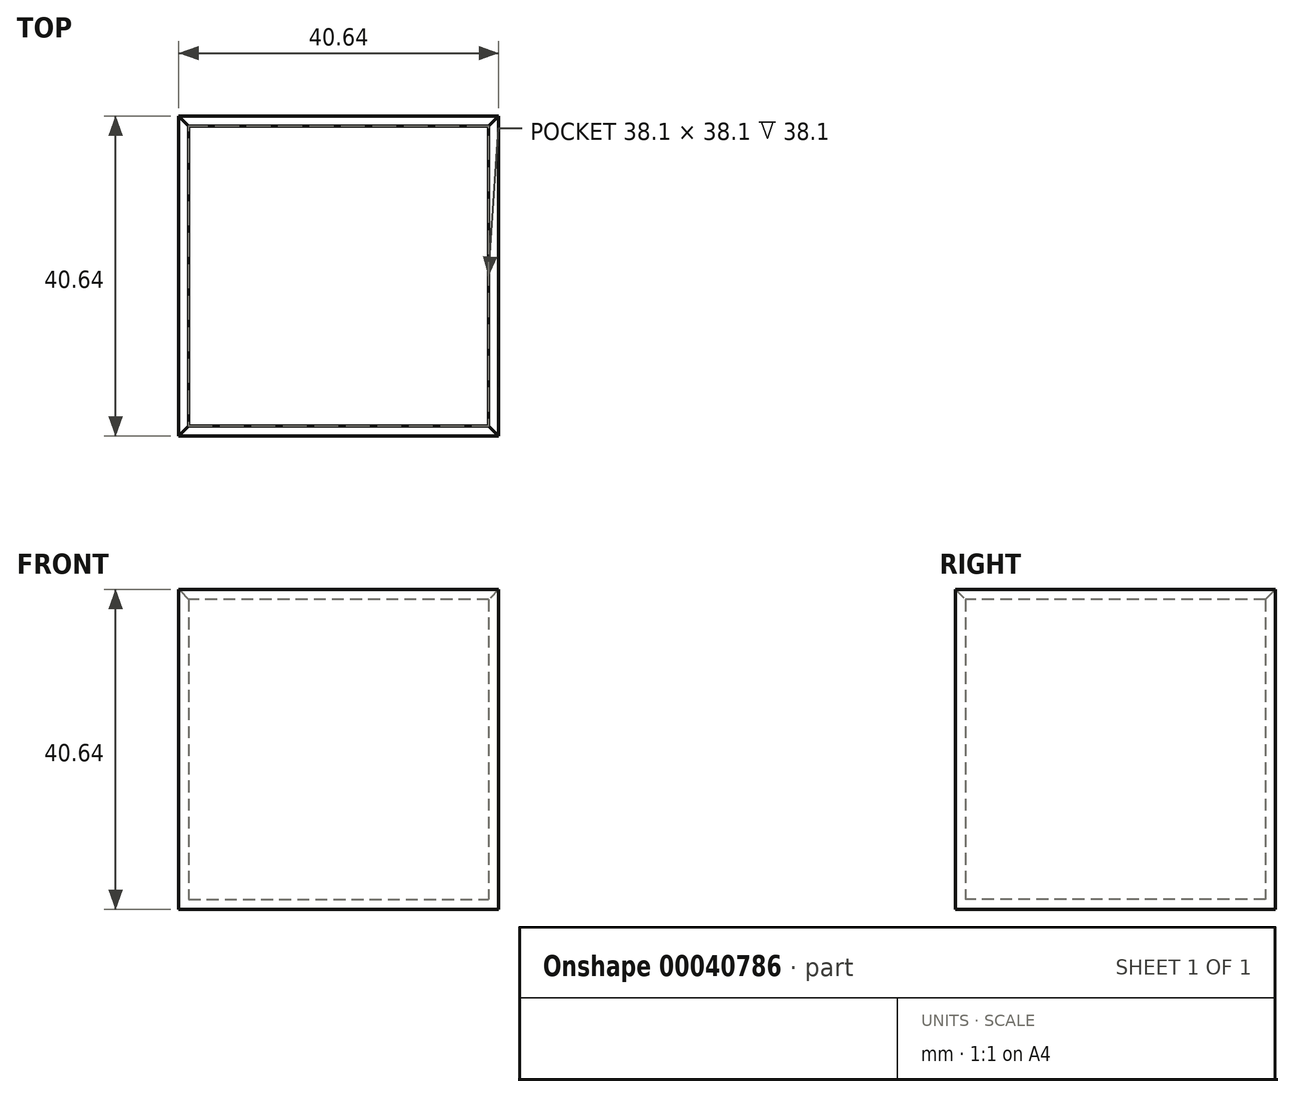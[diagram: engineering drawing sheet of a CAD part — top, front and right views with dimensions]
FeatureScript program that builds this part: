
annotation { "Feature Type Name" : "Feature", "Feature Type Description" : "" }
export const myFeature = defineFeature(function(context is Context, id is Id, definition is map)
    precondition{}
    {
        {
            var Q0;
            Q0=qCreatedBy(makeId("Top.planeOp"),FACE);
            var sketch = newSketch(context, id + "F0", { "sketchPlane" : qUnion([Q0])});
            skLineSegment(sketch, "E0.bottom", {"start": v(-21.61, 28.5) * mm, "end": v(19.03, 28.5) * mm});
            skLineSegment(sketch, "E0.top", {"start": v(-21.61, -12.14) * mm, "end": v(19.03, -12.14) * mm});
            skLineSegment(sketch, "E0.left", {"start": v(-21.61, 28.5) * mm, "end": v(-21.61, -12.14) * mm});
            skLineSegment(sketch, "E0.right", {"start": v(19.03, 28.5) * mm, "end": v(19.03, -12.14) * mm});
            skSolve(sketch);
        }
        {
            var Q0;
            Q0=makeQuery(id+"F0.imprint","IMPRINT",FACE,{"disambiguationData":[TD([[makeQuery(id+"F0.imprint","IMPRINT",EDGE,{"derivedFrom":sQuery(id+"F0.wireOp",EDGE,"E0.bottom")}),-1.0]])]});
            extrude(context, id + "F1", {"entities" : qUnion([Q0]), "depth" : 44.45 * mm});
        }
        {
            var Q0;
            Q0=makeQuery(id+"F1.opExtrude","CAP_FACE",FACE,{"disambiguationData":[OSD([sQuery(id+"F0.wireOp",EDGE,"E0.bottom"),sQuery(id+"F0.wireOp",EDGE,"E0.top"),sQuery(id+"F0.wireOp",EDGE,"E0.left"),sQuery(id+"F0.wireOp",EDGE,"E0.right")])],"isStart":false});
            shell(context, id + "F2", {"entities" : qUnion([Q0]), "thickness" : 1.27 * mm});
        }
        {
            var Q0;
            {var subQ0=sQuery(id+"F0.wireOp",EDGE,"E0.left");Q0=makeQuery(id+"F2.opShell","OFFSET_EDGE",EDGE,{"disambiguationData":[OSD([subQ0]),TDD([makeQuery(id+"F1.opExtrude","CAP_EDGE",EDGE,{"disambiguationData":[OSD([subQ0])],"isStart":false})])]});}
            var Q1;
            {var subQ0=sQuery(id+"F0.wireOp",EDGE,"E0.bottom");Q1=makeQuery(id+"F2.opShell","OFFSET_EDGE",EDGE,{"disambiguationData":[OSD([subQ0]),TDD([makeQuery(id+"F1.opExtrude","CAP_EDGE",EDGE,{"disambiguationData":[OSD([subQ0])],"isStart":false})])]});}
            var Q2;
            {var subQ0=sQuery(id+"F0.wireOp",EDGE,"E0.right");Q2=makeQuery(id+"F2.opShell","OFFSET_EDGE",EDGE,{"disambiguationData":[OSD([subQ0]),TDD([makeQuery(id+"F1.opExtrude","CAP_EDGE",EDGE,{"disambiguationData":[OSD([subQ0])],"isStart":false})])]});}
            var Q3;
            {var subQ0=sQuery(id+"F0.wireOp",EDGE,"E0.top");Q3=makeQuery(id+"F2.opShell","OFFSET_EDGE",EDGE,{"disambiguationData":[OSD([subQ0]),TDD([makeQuery(id+"F1.opExtrude","CAP_EDGE",EDGE,{"disambiguationData":[OSD([subQ0])],"isStart":false})])]});}
            chamfer(context, id + "F3", {"entities" : qUnion([Q0, Q1, Q2, Q3]), "width" : 5.08 * mm, "tangentPropagation" : true});
        }
    });
